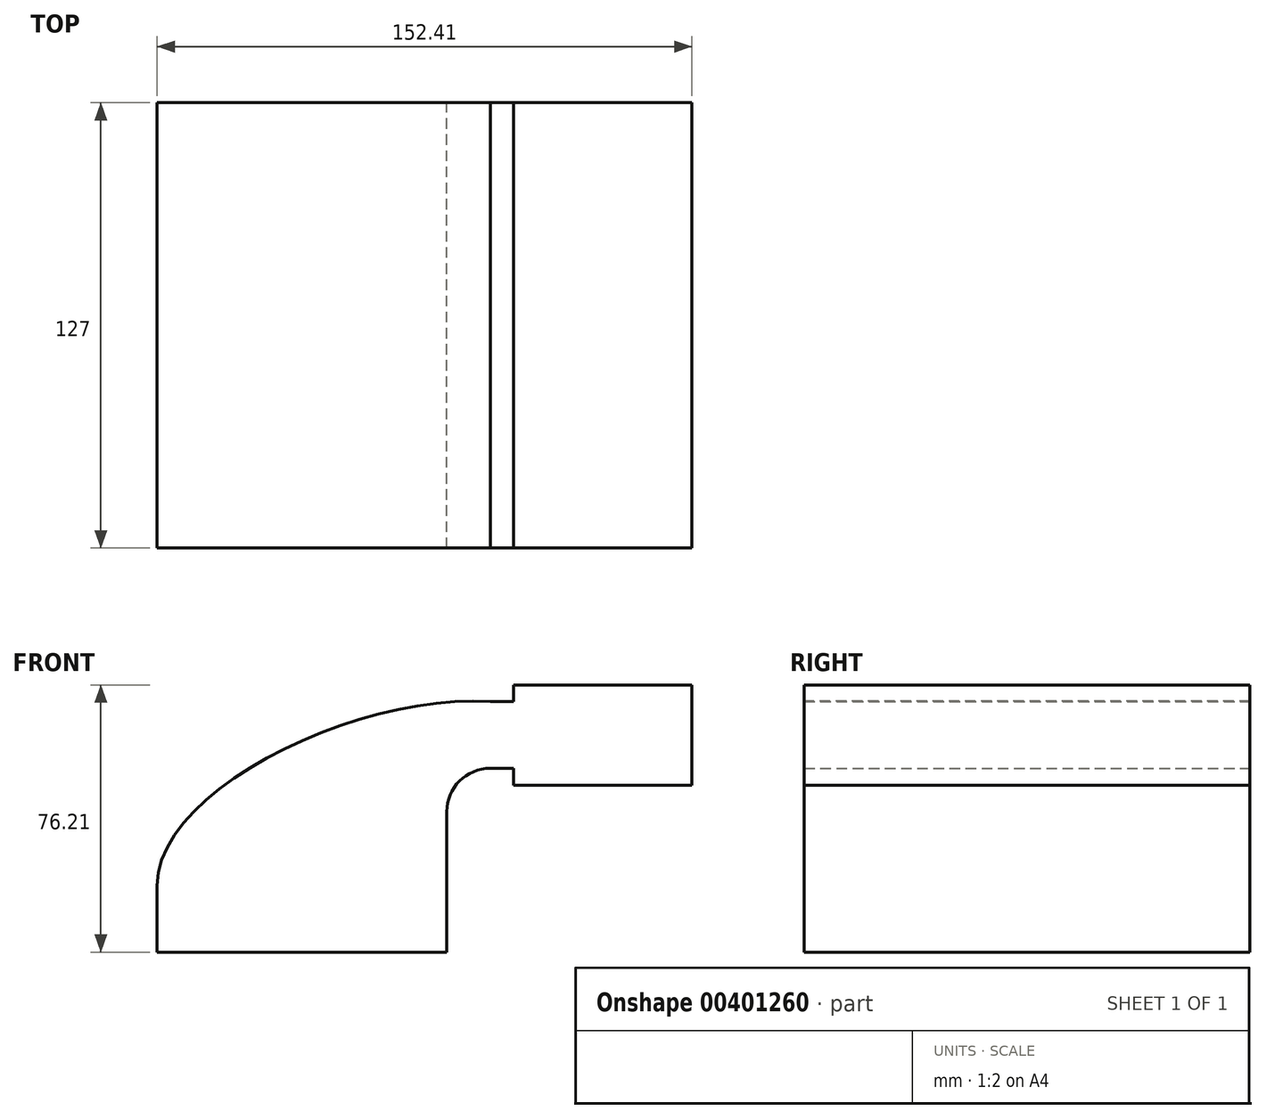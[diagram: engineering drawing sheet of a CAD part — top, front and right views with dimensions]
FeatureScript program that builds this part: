
annotation { "Feature Type Name" : "Feature", "Feature Type Description" : "" }
export const myFeature = defineFeature(function(context is Context, id is Id, definition is map)
    precondition{}
    {
        {
            var Q0;
            Q0=qCreatedBy(makeId("Front.planeOp"),FACE);
            var sketch = newSketch(context, id + "F0", { "sketchPlane" : qUnion([Q0])});
            skLineSegment(sketch, "E0.bottom", {"start": v(-41.28, 9.52) * mm, "end": v(41.27, 9.53) * mm});
            skLineSegment(sketch, "E0.top", {"start": v(-41.28, -9.53) * mm, "end": v(41.28, -9.53) * mm});
            skLineSegment(sketch, "E0.left", {"start": v(-41.28, 9.52) * mm, "end": v(-41.28, -9.53) * mm});
            skLineSegment(sketch, "E0.right", {"start": v(41.27, 9.53) * mm, "end": v(41.28, -9.52) * mm});
            skPoint(sketch, "E0.middle", {"position": v(0, 0) * mm});
            skLineSegment(sketch, "E1.bottom", {"start": v(111.12, 66.67) * mm, "end": v(60.32, 66.67) * mm});
            skLineSegment(sketch, "E1.top", {"start": v(111.12, 38.1) * mm, "end": v(60.32, 38.1) * mm});
            skLineSegment(sketch, "E1.left", {"start": v(111.12, 66.67) * mm, "end": v(111.12, 38.1) * mm});
            skLineSegment(sketch, "E1.right", {"start": v(60.32, 66.67) * mm, "end": v(60.32, 38.1) * mm});
            skPoint(sketch, "E1.middle", {"position": v(85.72, 52.39) * mm});
            skLineSegment(sketch, "E2", {"start": v(41.27, 9.53) * mm, "end": v(41.27, 30.52) * mm});
            skLineSegment(sketch, "E3", {"start": v(85.66, 42.88) * mm, "end": v(53.63, 42.88) * mm});
            skArc(sketch, "E4", {"start": v(41.27, 30.52) * mm, "mid": v(44.9, 39.26) * mm, "end": v(53.63, 42.88) * mm});
            skLineSegment(sketch, "E5.0", {"start": v(22.22, 9.53) * mm, "end": v(22.22, 30.52) * mm});
            skArc(sketch, "E5.1", {"start": v(22.22, 30.52) * mm, "mid": v(31.42, 52.73) * mm, "end": v(53.63, 61.93) * mm});
            skLineSegment(sketch, "E5.2", {"start": v(85.66, 61.93) * mm, "end": v(53.63, 61.93) * mm});
            skLineSegment(sketch, "E6", {"start": v(85.72, 38.1) * mm, "end": v(85.72, 66.67) * mm});
            skFitSpline(sketch, "E7", {"points": [v(-41.28, 9.52) * mm, v(53.63, 61.93) * mm], "startDerivative": vector(0.56, 83.24) * mm, "endDerivative": vector(110.71, -7.58) * mm});
            skSolve(sketch);
        }
        {
            var Q0;
            Q0 = qSketchRegion(id + "F0", true);
            extrude(context, id + "F1", {"entities" : qUnion([Q0]), "endBound" : BoundingType.SYMMETRIC, "depth" : 127 * mm});
        }
    });
